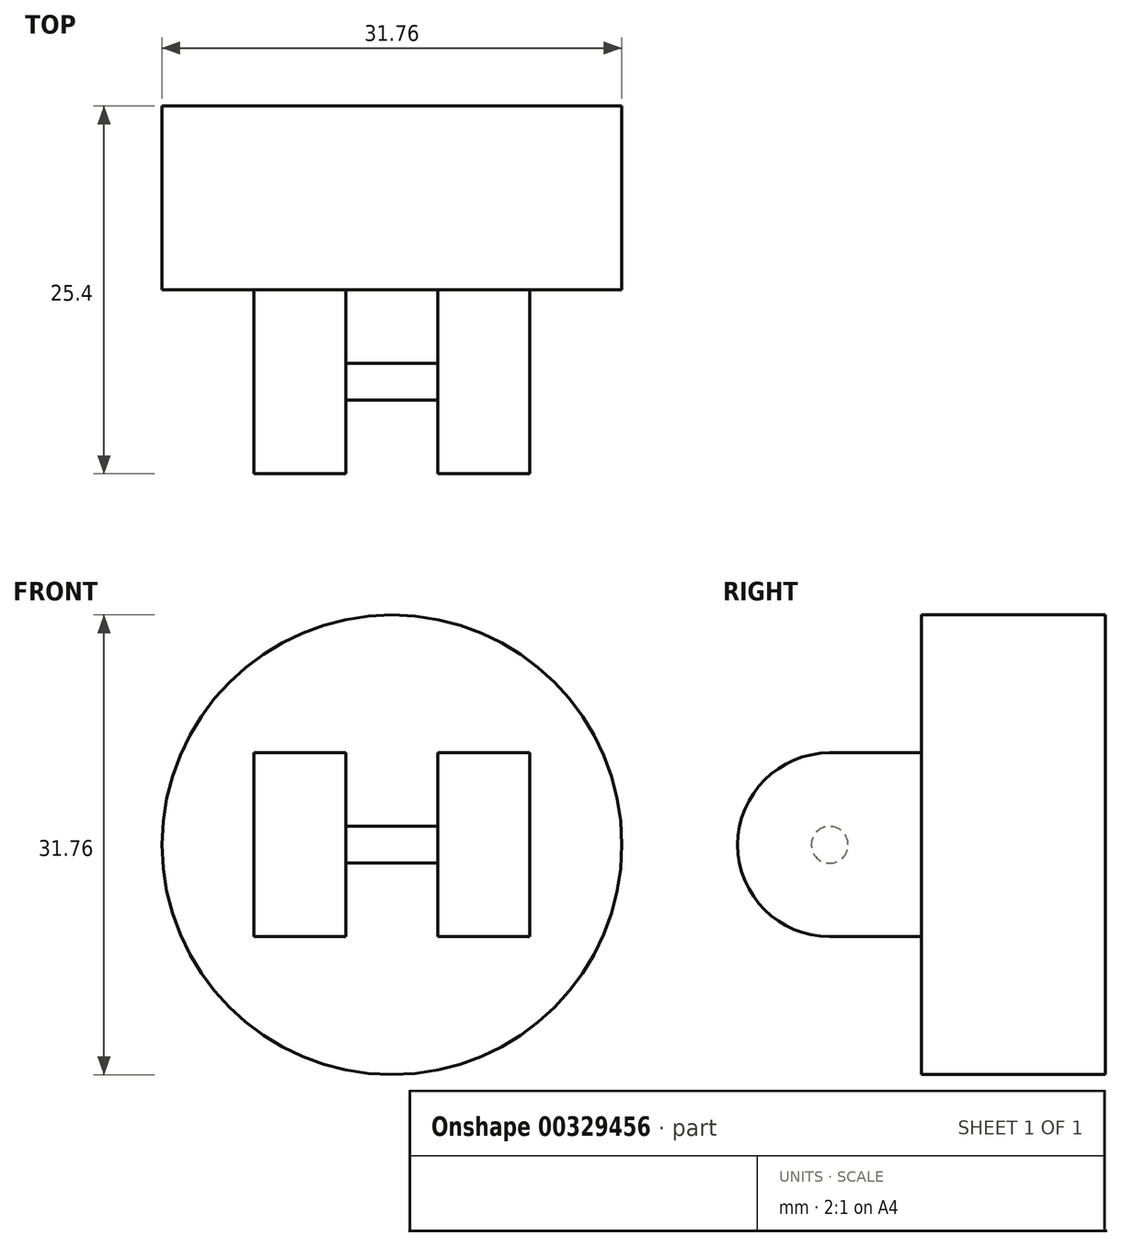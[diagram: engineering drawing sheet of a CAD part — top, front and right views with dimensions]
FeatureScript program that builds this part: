
annotation { "Feature Type Name" : "Feature", "Feature Type Description" : "" }
export const myFeature = defineFeature(function(context is Context, id is Id, definition is map)
    precondition{}
    {
        {
            var Q0;
            Q0=qCreatedBy(makeId("Front.planeOp"),FACE);
            var sketch = newSketch(context, id + "F0", { "sketchPlane" : qUnion([Q0])});
            skCircle(sketch, "E0", {"center": v(0, 0) * mm, "radius": 15.88 * mm});
            skSolve(sketch);
        }
        {
            var Q0;
            Q0 = qSketchRegion(id + "F0", true);
            extrude(context, id + "F1", {"entities" : qUnion([Q0]), "oppositeDirection" : true, "depth" : 12.7 * mm});
        }
        {
            var Q0;
            Q0=makeQuery(id+"F1.opExtrude","CAP_FACE",FACE,{"disambiguationData":[OSD([sQuery(id+"F0.wireOp",EDGE,"E0")])],"isStart":true});
            var sketch = newSketch(context, id + "F2", { "sketchPlane" : qUnion([Q0])});
            skLineSegment(sketch, "E1.bottom", {"start": v(-9.53, 6.35) * mm, "end": v(-3.18, 6.35) * mm});
            skLineSegment(sketch, "E1.top", {"start": v(-9.53, -6.35) * mm, "end": v(-3.17, -6.35) * mm});
            skLineSegment(sketch, "E1.left", {"start": v(-9.53, 6.35) * mm, "end": v(-9.53, -6.35) * mm});
            skLineSegment(sketch, "E1.right", {"start": v(-3.18, 6.35) * mm, "end": v(-3.17, -6.35) * mm});
            skLineSegment(sketch, "E2.bottom", {"start": v(3.17, 6.35) * mm, "end": v(9.53, 6.35) * mm});
            skLineSegment(sketch, "E2.top", {"start": v(3.18, -6.35) * mm, "end": v(9.53, -6.35) * mm});
            skLineSegment(sketch, "E2.left", {"start": v(3.17, 6.35) * mm, "end": v(3.18, -6.35) * mm});
            skLineSegment(sketch, "E2.right", {"start": v(9.53, 6.35) * mm, "end": v(9.53, -6.35) * mm});
            skSolve(sketch);
        }
        {
            var Q0;
            Q0 = qSketchRegion(id + "F2", true);
            extrude(context, id + "F3", {"entities" : qUnion([Q0]), "operationType" : NewBodyOperationType.ADD, "depth" : 12.7 * mm});
        }
        {
            var Q0;
            Q0=makeQuery(id+"F3.opExtrude","CAP_EDGE",EDGE,{"disambiguationData":[OSD([sQuery(id+"F2.wireOp",EDGE,"E1.bottom")])],"isStart":false});
            var Q1;
            Q1=makeQuery(id+"F3.opExtrude","CAP_EDGE",EDGE,{"disambiguationData":[OSD([sQuery(id+"F2.wireOp",EDGE,"E2.bottom")])],"isStart":false});
            var Q2;
            Q2=makeQuery(id+"F3.opExtrude","CAP_EDGE",EDGE,{"disambiguationData":[OSD([sQuery(id+"F2.wireOp",EDGE,"E1.top")])],"isStart":false});
            var Q3;
            Q3=makeQuery(id+"F3.opExtrude","CAP_EDGE",EDGE,{"disambiguationData":[OSD([sQuery(id+"F2.wireOp",EDGE,"E2.top")])],"isStart":false});
            fillet(context, id + "F4", {"entities" : qUnion([Q0, Q1, Q2, Q3]), "radius" : 6.35 * mm, "tangentPropagation" : true, "allowEdgeOverflow" : false});
        }
        {
            var Q0;
            Q0=makeQuery(id+"F3.opExtrude","SWEPT_FACE",FACE,{"disambiguationData":[OSD([sQuery(id+"F2.wireOp",EDGE,"E2.right")])]});
            var sketch = newSketch(context, id + "F5", { "sketchPlane" : qUnion([Q0])});
            skCircle(sketch, "E3", {"center": v(-6.35, 0) * mm, "radius": 1.27 * mm});
            skSolve(sketch);
        }
        {
            var Q0;
            Q0 = qSketchRegion(id + "F5", true);
            extrude(context, id + "F6", {"entities" : qUnion([Q0]), "operationType" : NewBodyOperationType.ADD, "oppositeDirection" : true, "depth" : 19.05 * mm});
        }
    });
